# Revit family: Camera-Security-Panasonic-Super_Dynamic-Weatherproof-Network-SPW631L
name_source: partatom
category: Security Devices
revit_build: Autodesk Revit 2013 (Build: 20130531_2115(x64)
units: mm (PartAtom-declared; Revit-internal decimal feet)

## types (4) — shared parameters
Alarm Input Or Output Specification = ALARM IN 1 (DAY/NIGHT IN), ALARM IN 2 (ALARM OUT), ALARM IN 3 (AUX OUT)
Audio In = Yes
Audio Out = Yes
Communication Ports = 10Base-T / 100Base-TX, RJ-45
Date Last Modified = July, 20, 2016
Day Or Night = Yes
Default Elevation = 48 "
Equipment Abbreviation = SC
Family Version = 1.0.0
Has POE = Yes
IP Or Analog = IP
Indoor Or Outdoor = Outdoor
Manufacturer = Panasonic
Minimum Illumination = 0 lx
Model Disclaimer = Contact Panasonic for more information
Mounting Positions = Mount Dependent or Surface Mount
Operational Humidity = 10% to 90% (no condensation)
Operational Temperature = -40°F - 122°F
Panning Range = -100 to +100
Product Documentation Link = http://ssbu-t.psn-web.net
Product Material = Paint - Panasonic - Silver
Product Page URL = http://security.panasonic.com
Provide Feedback = https://www.surveymonkey.com
Regulatory Compliance = UL (UL60950-1), C-UL (CAN/CSA C22.2 No.60950-1), CE, IEC60950-1 FCC (Part15 ClassA), ICES003 ClassA, EN55022 ClassB, EN55024
Storage Temperature = -40°F - 122°F
Tilting Range = -90 to +30
URL = http://security.panasonic.com
Vandal Resistant = No
Voltage DC = 12 V
Weight = 3.09 lb
Wide Dynamic Range = Yes
zero-valued in all types: Cost

## per-type parameters (varying)
| type | Angle Of View | Description | Part Description | Power Active |
| WV-SPW611 | 96.2 | Super Dynamic HD Weatherproof Network Camera WV-SPW611 | Super Dynamic HD Weatherproof Network Camera WV-SPW611 | 8.1 W |
| WV-SPW611L | 96.2 | Super Dynamic HD Weatherproof Network Camera WV-SPW611L | Super Dynamic HD Weatherproof Network Camera WV-SPW611L | 12.9 W |
| WV-SPW631L | 105.4 | Super Dynamic Full HD Weatherproof Network Camera WV-SPW631L | Super Dynamic Full HD Weatherproof Network Camera WV-SPW631L | 12.9 W |
| WV-SPW631LT | 33.5 | Super Dynamic Full HD Weatherproof Long Focus Type Network Camera WV-SPW631LT | Super Dynamic Full HD Weatherproof Long Focus Type Network Camera WV-SPW631LT | 12.9 W |

note: column(s) folded — value = type name in every type: Model, Part Number

## geometry (parser evidence)
native form markers: Blend x8, Extrusion x3, Sweep x10
no freeform markers — native parametric forms only
